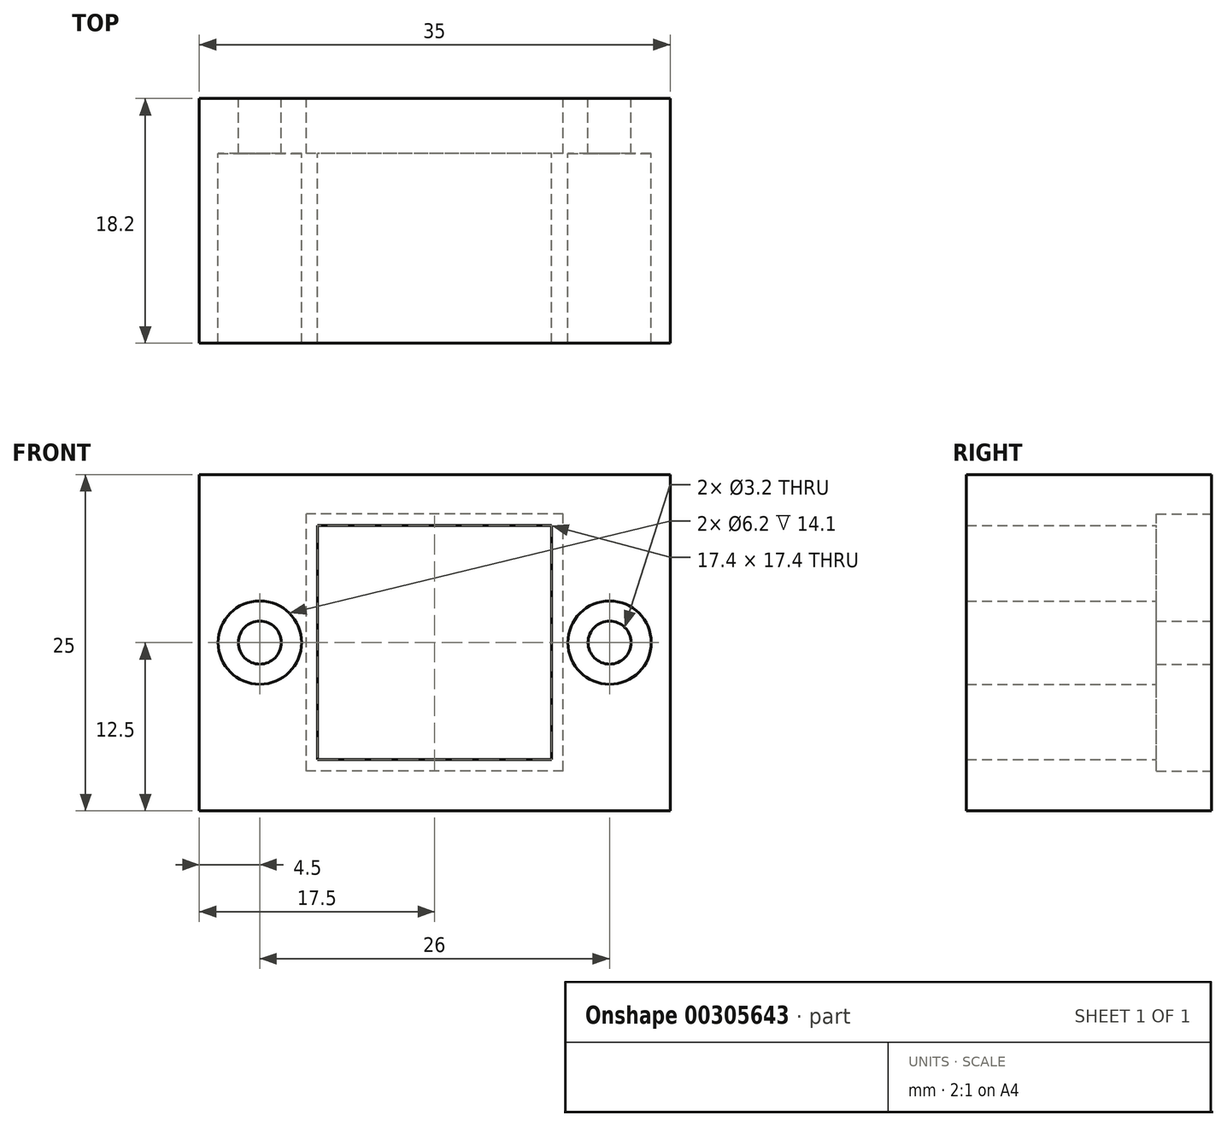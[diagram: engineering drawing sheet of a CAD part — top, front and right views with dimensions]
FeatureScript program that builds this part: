
annotation { "Feature Type Name" : "Feature", "Feature Type Description" : "" }
export const myFeature = defineFeature(function(context is Context, id is Id, definition is map)
    precondition{}
    {
        {
            var Q0;
            Q0=qCreatedBy(makeId("Front.planeOp"),FACE);
            var sketch = newSketch(context, id + "F0", { "sketchPlane" : qUnion([Q0])});
            skLineSegment(sketch, "E0.bottom", {"start": v(9.55, -9.55) * mm, "end": v(-9.55, -9.55) * mm});
            skLineSegment(sketch, "E0.top", {"start": v(9.55, 9.55) * mm, "end": v(-9.55, 9.55) * mm});
            skLineSegment(sketch, "E0.left", {"start": v(9.55, -9.55) * mm, "end": v(9.55, 9.55) * mm});
            skLineSegment(sketch, "E0.right", {"start": v(-9.55, -9.55) * mm, "end": v(-9.55, 9.55) * mm});
            skPoint(sketch, "E0.middle", {"position": v(0, 0) * mm});
            skCircle(sketch, "E1", {"center": v(-13, 0) * mm, "radius": 1.6 * mm});
            skCircle(sketch, "E2", {"center": v(13, 0) * mm, "radius": 1.6 * mm});
            skLineSegment(sketch, "E3.bottom", {"start": v(17.5, -12.5) * mm, "end": v(-17.5, -12.5) * mm});
            skLineSegment(sketch, "E3.top", {"start": v(17.5, 12.5) * mm, "end": v(-17.5, 12.5) * mm});
            skLineSegment(sketch, "E3.left", {"start": v(17.5, -12.5) * mm, "end": v(17.5, 12.5) * mm});
            skLineSegment(sketch, "E3.right", {"start": v(-17.5, -12.5) * mm, "end": v(-17.5, 12.5) * mm});
            skSolve(sketch);
        }
        {
            var Q0;
            Q0=makeQuery(id+"F0.imprint","IMPRINT",FACE,{"disambiguationData":[TD([[makeQuery(id+"F0.imprint","IMPRINT",EDGE,{"derivedFrom":sQuery(id+"F0.wireOp",EDGE,"E0.bottom")}),1.0]])]});
            extrude(context, id + "F1", {"entities" : qUnion([Q0]), "depth" : 4.1 * mm});
        }
        {
            var Q0;
            Q0=makeQuery(id+"F1.opExtrude","CAP_FACE",FACE,{"disambiguationData":[OSD([sQuery(id+"F0.wireOp",EDGE,"E0.bottom"),sQuery(id+"F0.wireOp",EDGE,"E0.top"),sQuery(id+"F0.wireOp",EDGE,"E0.left"),sQuery(id+"F0.wireOp",EDGE,"E0.right"),sQuery(id+"F0.wireOp",EDGE,"E1"),sQuery(id+"F0.wireOp",EDGE,"E2"),sQuery(id+"F0.wireOp",EDGE,"E3.bottom"),sQuery(id+"F0.wireOp",EDGE,"E3.top"),sQuery(id+"F0.wireOp",EDGE,"E3.left"),sQuery(id+"F0.wireOp",EDGE,"E3.right")])],"isStart":false});
            var sketch = newSketch(context, id + "F2", { "sketchPlane" : qUnion([Q0])});
            skLineSegment(sketch, "E4.bottom", {"start": v(8.7, -8.7) * mm, "end": v(-8.7, -8.7) * mm});
            skLineSegment(sketch, "E4.top", {"start": v(8.7, 8.7) * mm, "end": v(-8.7, 8.7) * mm});
            skLineSegment(sketch, "E4.left", {"start": v(8.7, -8.7) * mm, "end": v(8.7, 8.7) * mm});
            skLineSegment(sketch, "E4.right", {"start": v(-8.7, -8.7) * mm, "end": v(-8.7, 8.7) * mm});
            skPoint(sketch, "E4.middle", {"position": v(0, 0) * mm});
            skLineSegment(sketch, "E5.bottom", {"start": v(17.5, -12.5) * mm, "end": v(-17.5, -12.5) * mm});
            skLineSegment(sketch, "E5.top", {"start": v(17.5, 12.5) * mm, "end": v(-17.5, 12.5) * mm});
            skLineSegment(sketch, "E5.left", {"start": v(17.5, -12.5) * mm, "end": v(17.5, 12.5) * mm});
            skLineSegment(sketch, "E5.right", {"start": v(-17.5, -12.5) * mm, "end": v(-17.5, 12.5) * mm});
            skCircle(sketch, "E6", {"center": v(-13, 0) * mm, "radius": 3.1 * mm});
            skCircle(sketch, "E7", {"center": v(13, 0) * mm, "radius": 3.1 * mm});
            skSolve(sketch);
        }
        {
            var Q0;
            Q0=qSketchRegion(id+"F2",true);
            extrude(context, id + "F3", {"entities" : qUnion([Q0]), "operationType" : NewBodyOperationType.ADD, "depth" : 14.1 * mm});
        }
    });
